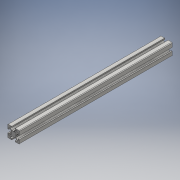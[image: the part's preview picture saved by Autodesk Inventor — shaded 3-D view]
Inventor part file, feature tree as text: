
AUTODESK INVENTOR PART (.ipt)
format: ipt  version: 2016 (Build 200138000, 138)  size: 176,640 bytes
history: native  units: mm
features: other x1, extrude x1, sketch x1
ambient origin geometry x8: Origin, YZ Plane, XZ Plane, XY Plane, X Axis, Y Axis, Z Axis, Center Point
bodies: Body1 (feature_tree)
feature tree (3):
  other  "ソリッド1"
  extrude  "押し出し1"  Depth=260.0mm TaperAngle=0.0deg
  sketch  "スケッチ1"
